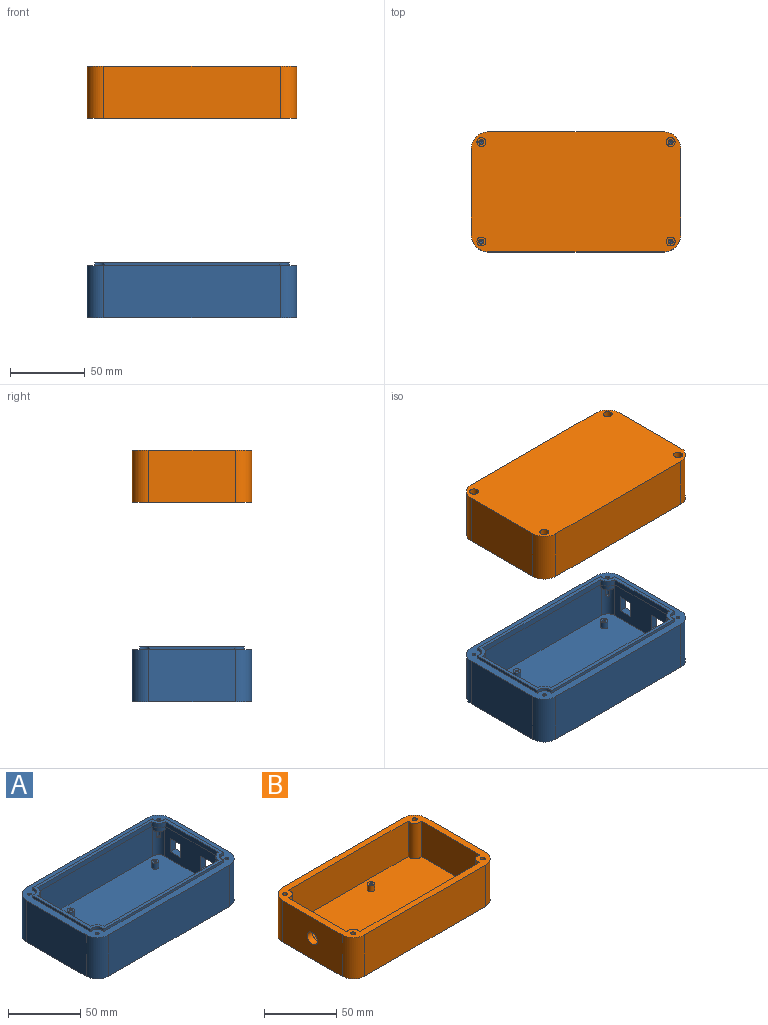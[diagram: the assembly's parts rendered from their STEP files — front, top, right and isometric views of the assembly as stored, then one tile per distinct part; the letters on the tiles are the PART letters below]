
ASSEMBLY  parts=2 mates=1
PART A: 77 faces, bbox 140x80x37 mm
  f0: plane 58x35mm, normal (1,0,0), area 1780.5mm2, adj f6,f12,f13,f14,f61,f62,f63,f64
  f1: plane 58x28mm, normal (-1,0,0), area 1370.1mm2, adj f2,f4,f32,f33,f34,f36,f38,f39
  f2: cylinder r=6mm len=23mm, axis (0,0,-1), area 195.8mm2, adj f1,f33,f36,f44,f47,f48
  f3: cylinder r=6mm len=23mm, axis (0,0,-1), area 195.8mm2, adj f33,f37,f43,f44,f45,f46
  f4: cylinder r=6mm len=23mm, axis (0,0,-1), area 195.8mm2, adj f1,f33,f34,f41,f51,f52
  f5: cylinder r=6mm len=23mm, axis (0,0,-1), area 195.8mm2, adj f33,f35,f41,f43,f49,f50
  f6: cylinder r=11mm len=35mm, axis (0,0,1), area 604.8mm2, adj f0,f7,f13,f14
  f7: plane 118x35mm, normal (0,1,0), area 4130mm2, adj f6,f8,f13,f14
  f8: cylinder r=11mm len=35mm, axis (0,0,1), area 604.8mm2, adj f7,f9,f13,f14
  f9: plane 58x35mm, normal (-1,0,0), area 2030mm2, adj f8,f10,f13,f14
  f10: cylinder r=11mm len=35mm, axis (0,0,1), area 604.8mm2, adj f9,f11,f13,f14
  f11: plane 118x35mm, normal (0,-1,0), area 4130mm2, adj f10,f12,f13,f14
  f12: cylinder r=11mm len=35mm, axis (0,0,1), area 604.8mm2, adj f0,f11,f13,f14
  f13: plane 140x80mm, normal (0,0,-1), area 11096.1mm2, adj f0,f6,f7,f8,f9,f10,f11,f12
  f14: plane 140x80mm, normal (0,0,1), area 2136.2mm2, adj f0,f6,f7,f8,f9,f10,f11,f12
  f15: plane 51.56x4mm, normal (1,0,0), area 206.2mm2, adj f16,f30,f31,f32
  f16: cylinder r=7.5mm len=6.72mm, axis (0,0,-1), area 41.2mm2, adj f15,f17,f31,f32
  f17: plane 111.56x4mm, normal (0,-1,0), area 446.2mm2, adj f16,f18,f31,f32
  f18: cylinder r=7.5mm len=6.72mm, axis (0,0,-1), area 41.2mm2, adj f17,f19,f31,f32
  f19: plane 51.56x4mm, normal (-1,0,0), area 206.2mm2, adj f18,f20,f31,f32
  f20: cylinder r=7.5mm len=6.72mm, axis (0,0,-1), area 41.2mm2, adj f19,f21,f31,f32
  f21: plane 111.56x4mm, normal (0,1,0), area 446.2mm2, adj f20,f30,f31,f32
  f22: cylinder r=5mm len=6.76mm, axis (0,0,-1), area 22.9mm2, adj f14,f23,f29,f31
  f23: plane 117.12x2mm, normal (0,-1,0), area 234.2mm2, adj f14,f22,f24,f31
  f24: cylinder r=5mm len=6.76mm, axis (0,0,-1), area 22.9mm2, adj f14,f23,f25,f31
  f25: plane 57.12x2mm, normal (1,0,0), area 114.2mm2, adj f14,f24,f26,f31
  f26: cylinder r=5mm len=6.76mm, axis (0,0,-1), area 22.9mm2, adj f14,f25,f27,f31
  f27: plane 117.12x2mm, normal (0,1,0), area 234.2mm2, adj f14,f26,f28,f31
  f28: cylinder r=5mm len=6.76mm, axis (0,0,-1), area 22.9mm2, adj f14,f27,f29,f31
  f29: plane 57.12x2mm, normal (-1,0,0), area 114.2mm2, adj f14,f22,f28,f31
  f30: cylinder r=7.5mm len=6.72mm, axis (0,0,-1), area 41.2mm2, adj f15,f21,f31,f32
  f31: plane 130x70mm, normal (0,0,1), area 949.7mm2, adj f15,f16,f17,f18,f19,f20,f21,f22
  f32: plane 130x70mm, normal (0,0,-1), area 949.7mm2, adj f1,f15,f16,f17,f18,f19,f20,f21
  f33: plane 130x70mm, normal (0,0,1), area 8990.6mm2, adj f1,f2,f3,f4,f5,f41,f43,f44
  f34: plane 6.76x6.76mm, normal (0,0,-1), area 29.9mm2, adj f1,f4,f39,f41,f52
  f35: plane 6.76x6.76mm, normal (0,0,-1), area 29.9mm2, adj f5,f40,f41,f43,f50
  f36: plane 6.76x6.76mm, normal (0,0,-1), area 29.9mm2, adj f1,f2,f38,f44,f48
  f37: plane 6.76x6.76mm, normal (0,0,-1), area 29.9mm2, adj f3,f42,f43,f44,f46
  f38: cylinder r=5mm len=6.76mm, axis (0,0,1), area 57.2mm2, adj f1,f32,f36,f44
  f39: cylinder r=5mm len=6.76mm, axis (0,0,1), area 57.2mm2, adj f1,f32,f34,f41
  f40: cylinder r=5mm len=6.76mm, axis (0,0,1), area 57.2mm2, adj f32,f35,f41,f43
  f41: plane 118x28mm, normal (0,-1,0), area 3299.6mm2, adj f4,f5,f32,f33,f34,f35,f39,f40
  f42: cylinder r=5mm len=6.76mm, axis (0,0,1), area 57.2mm2, adj f32,f37,f43,f44
  f43: plane 58x28mm, normal (1,0,0), area 1619.6mm2, adj f3,f5,f32,f33,f35,f37,f40,f42
  f44: plane 118x28mm, normal (0,1,0), area 3299.6mm2, adj f2,f3,f32,f33,f36,f37,f38,f42
  f45: cone r=0mm half-angle=59deg, axis (0,0,1), area 3mm2, adj f3,f46
  f46: cylinder r=1.25mm len=15mm, axis (0,0,1), area 88.5mm2, adj f3,f14,f37,f45
  f47: cone r=0mm half-angle=59deg, axis (0,0,1), area 3mm2, adj f2,f48
  f48: cylinder r=1.25mm len=15mm, axis (0,0,1), area 88.5mm2, adj f2,f14,f36,f47
  f49: cone r=0mm half-angle=59deg, axis (0,0,1), area 3mm2, adj f5,f50
  f50: cylinder r=1.25mm len=15mm, axis (0,0,1), area 88.5mm2, adj f5,f14,f35,f49
  f51: cone r=0mm half-angle=59deg, axis (0,0,1), area 3mm2, adj f4,f52
  f52: cylinder r=1.25mm len=15mm, axis (0,0,1), area 88.5mm2, adj f4,f14,f34,f51
  f53: cylinder r=2.5mm len=5mm, axis (0,0,-1), area 78.5mm2, adj f33,f54
  f54: plane 5x5mm, normal (0,0,1), area 16.3mm2, adj f53,f76
  f55: cylinder r=2.5mm len=5mm, axis (0,0,-1), area 78.5mm2, adj f33,f56
  f56: plane 5x5mm, normal (0,0,1), area 16.3mm2, adj f55,f74
  f57: cylinder r=2.5mm len=5mm, axis (0,0,-1), area 78.5mm2, adj f33,f58
  f58: plane 5x5mm, normal (0,0,1), area 16.3mm2, adj f57,f72
  f59: cylinder r=2.5mm len=5mm, axis (0,0,-1), area 78.5mm2, adj f33,f60
  f60: plane 5x5mm, normal (0,0,1), area 16.3mm2, adj f59,f70
  f61: plane 11.2x5mm, normal (0,1,0), area 56mm2, adj f0,f1,f62,f64
  f62: plane 10x5mm, normal (0,0,1), area 50mm2, adj f0,f1,f61,f63
  f63: plane 11.2x5mm, normal (0,-1,0), area 56mm2, adj f0,f1,f62,f64
  f64: plane 10x5mm, normal (0,0,-1), area 50mm2, adj f0,f1,f61,f63
  f65: plane 11x5mm, normal (0,1,0), area 55mm2, adj f0,f1,f66,f68
  f66: plane 12.5x5mm, normal (0,0,1), area 62.5mm2, adj f0,f1,f65,f67
  f67: plane 11x5mm, normal (0,-1,0), area 55mm2, adj f0,f1,f66,f68
  f68: plane 12.5x5mm, normal (0,0,-1), area 62.5mm2, adj f0,f1,f65,f67
  f69: plane 2.05x2.05mm, normal (0,0,1), area 3.3mm2, adj f70
  f70: cylinder r=1.03mm len=5mm, axis (0,0,-1), area 32.2mm2, adj f60,f69
  f71: plane 2.05x2.05mm, normal (0,0,1), area 3.3mm2, adj f72
  f72: cylinder r=1.03mm len=5mm, axis (0,0,-1), area 32.2mm2, adj f58,f71
  f73: plane 2.05x2.05mm, normal (0,0,1), area 3.3mm2, adj f74
  f74: cylinder r=1.03mm len=5mm, axis (0,0,-1), area 32.2mm2, adj f56,f73
  f75: plane 2.05x2.05mm, normal (0,0,1), area 3.3mm2, adj f76
  f76: cylinder r=1.03mm len=5mm, axis (0,0,-1), area 32.2mm2, adj f54,f75
PART B: 48 faces, bbox 140x80x35 mm
  f0: cylinder r=2.5mm len=5mm, axis (0,0,-1), area 78.5mm2, adj f1,f20
  f1: plane 5x5mm, normal (0,0,1), area 16.3mm2, adj f0,f47
  f2: cylinder r=1.7mm len=10mm, axis (0,0,1), area 106.8mm2, adj f19,f32
  f3: cylinder r=1.7mm len=10mm, axis (0,0,1), area 106.8mm2, adj f19,f30
  f4: cylinder r=1.7mm len=10mm, axis (0,0,1), area 106.8mm2, adj f19,f28
  f5: cylinder r=1.7mm len=10mm, axis (0,0,1), area 106.8mm2, adj f19,f26
  f6: plane 58x35mm, normal (-1,0,0), area 1951.5mm2, adj f7,f13,f14,f19,f39
  f7: cylinder r=11mm len=35mm, axis (0,0,1), area 604.8mm2, adj f6,f8,f14,f19
  f8: plane 118x35mm, normal (0,1,0), area 4130mm2, adj f7,f9,f14,f19
  f9: cylinder r=11mm len=35mm, axis (0,0,1), area 604.8mm2, adj f8,f10,f14,f19
  f10: plane 58x35mm, normal (1,0,0), area 2030mm2, adj f9,f11,f14,f19
  f11: cylinder r=11mm len=35mm, axis (0,0,1), area 604.8mm2, adj f10,f12,f14,f19
  f12: plane 118x35mm, normal (0,-1,0), area 4130mm2, adj f11,f13,f14,f19
  f13: cylinder r=11mm len=35mm, axis (0,0,1), area 604.8mm2, adj f6,f12,f14,f19
  f14: plane 140x80mm, normal (0,0,-1), area 10983mm2, adj f6,f7,f8,f9,f10,f11,f12,f13
  f15: plane 57.12x30mm, normal (1,0,0), area 1635.2mm2, adj f19,f20,f21,f22,f39
  f16: plane 117.12x30mm, normal (0,1,0), area 3513.7mm2, adj f19,f20,f21,f23
  f17: plane 57.12x30mm, normal (-1,0,0), area 1713.7mm2, adj f19,f20,f23,f24
  f18: plane 117.12x30mm, normal (0,-1,0), area 3513.7mm2, adj f19,f20,f22,f24
  f19: plane 140x80mm, normal (0,0,1), area 2119.5mm2, adj f2,f3,f4,f5,f6,f7,f8,f9
  f20: plane 130x70mm, normal (0,0,1), area 8861.7mm2, adj f0,f15,f16,f17,f18,f21,f22,f23
  f21: cylinder r=5mm len=30mm, axis (0,0,1), area 343.4mm2, adj f15,f16,f19,f20
  f22: cylinder r=5mm len=30mm, axis (0,0,1), area 343.4mm2, adj f15,f18,f19,f20
  f23: cylinder r=5mm len=30mm, axis (0,0,1), area 343.4mm2, adj f16,f17,f19,f20
  f24: cylinder r=5mm len=30mm, axis (0,0,1), area 343.4mm2, adj f17,f18,f19,f20
  f25: cylinder r=3mm len=25mm, axis (0,0,-1), area 471.2mm2, adj f14,f26
  f26: plane 6x6mm, normal (0,0,-1), area 19.2mm2, adj f5,f25
  f27: cylinder r=3mm len=25mm, axis (0,0,-1), area 471.2mm2, adj f14,f28
  f28: plane 6x6mm, normal (0,0,-1), area 19.2mm2, adj f4,f27
  f29: cylinder r=3mm len=25mm, axis (0,0,-1), area 471.2mm2, adj f14,f30
  f30: plane 6x6mm, normal (0,0,-1), area 19.2mm2, adj f3,f29
  f31: cylinder r=3mm len=25mm, axis (0,0,-1), area 471.2mm2, adj f14,f32
  f32: plane 6x6mm, normal (0,0,-1), area 19.2mm2, adj f2,f31
  f33: cylinder r=2.5mm len=5mm, axis (0,0,-1), area 78.5mm2, adj f20,f34
  f34: plane 5x5mm, normal (0,0,1), area 16.3mm2, adj f33,f45
  f35: cylinder r=2.5mm len=5mm, axis (0,0,-1), area 78.5mm2, adj f20,f36
  f36: plane 5x5mm, normal (0,0,1), area 16.3mm2, adj f35,f43
  f37: cylinder r=2.5mm len=5mm, axis (0,0,-1), area 78.5mm2, adj f20,f38
  f38: plane 5x5mm, normal (0,0,1), area 16.3mm2, adj f37,f41
  f39: cylinder r=5mm len=10mm, axis (-1,0,0), area 157.1mm2, adj f6,f15
  f40: plane 2.05x2.05mm, normal (0,0,1), area 3.3mm2, adj f41
  f41: cylinder r=1.03mm len=5mm, axis (0,0,-1), area 32.2mm2, adj f38,f40
  f42: plane 2.05x2.05mm, normal (0,0,1), area 3.3mm2, adj f43
  f43: cylinder r=1.03mm len=5mm, axis (0,0,-1), area 32.2mm2, adj f36,f42
  f44: plane 2.05x2.05mm, normal (0,0,1), area 3.3mm2, adj f45
  f45: cylinder r=1.03mm len=5mm, axis (0,0,-1), area 32.2mm2, adj f34,f44
  f46: plane 2.05x2.05mm, normal (0,0,1), area 3.3mm2, adj f47
  f47: cylinder r=1.03mm len=5mm, axis (0,0,-1), area 32.2mm2, adj f1,f46
PLACE A t=(-680.24,145.28,-84.25)mm
PLACE B rot(axis=(0,1,0),180deg) t=(-680.24,145.28,74.15)mm
MATE slider A.f14 <-> B.f19  axis (0,0,1) through (-606.01,184.49,-54.25)mm
